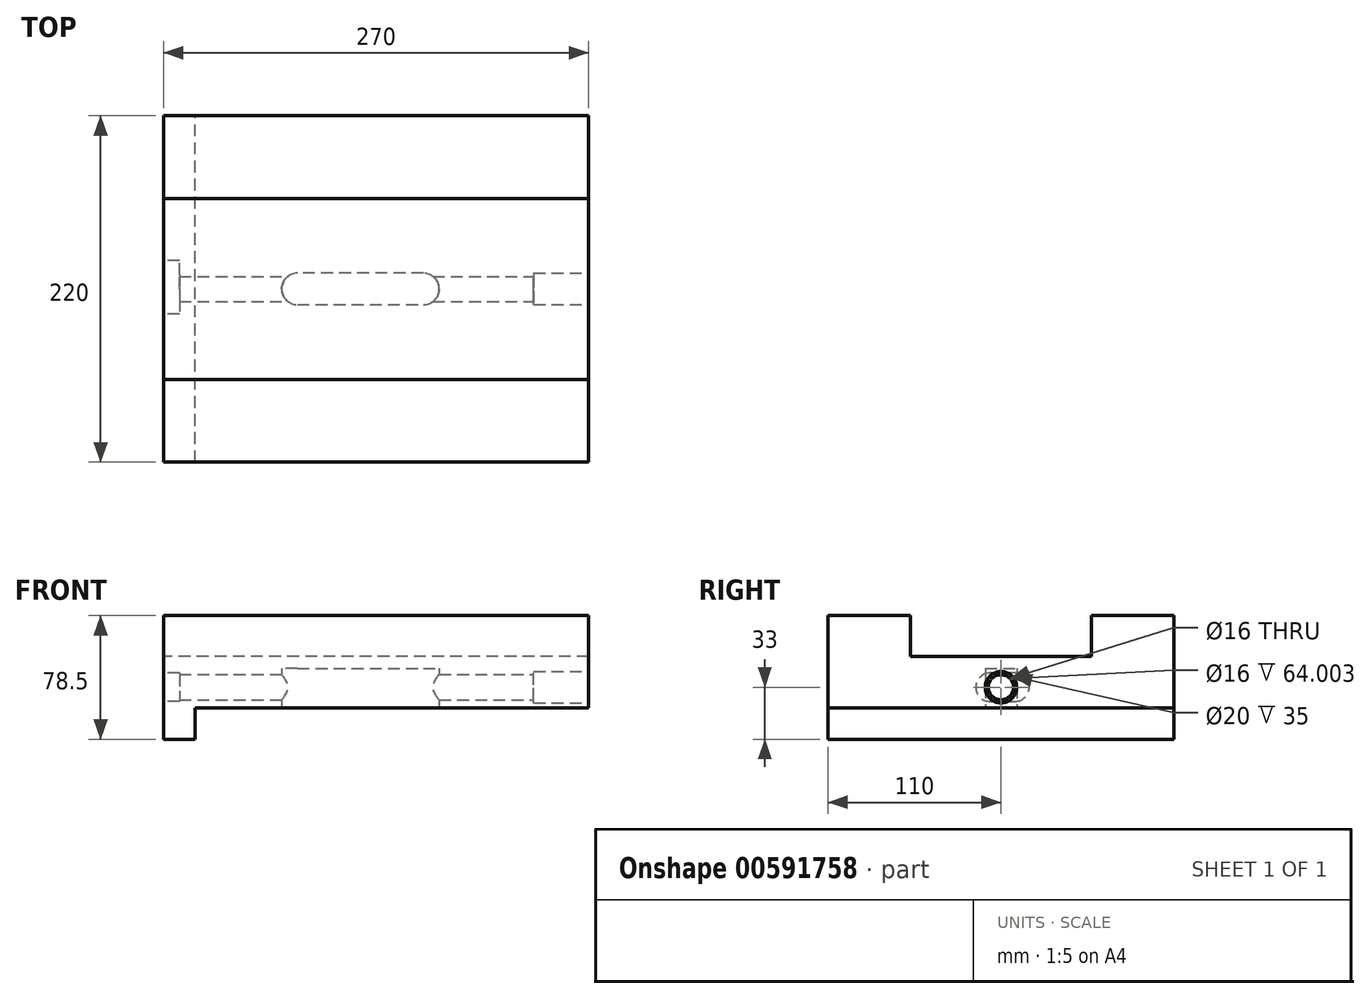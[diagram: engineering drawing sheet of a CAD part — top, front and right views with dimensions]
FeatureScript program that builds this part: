
annotation { "Feature Type Name" : "Feature", "Feature Type Description" : "" }
export const myFeature = defineFeature(function(context is Context, id is Id, definition is map)
    precondition{}
    {
        {
            var Q0;
            Q0=qCreatedBy(makeId("Front.planeOp"),FACE);
            var sketch = newSketch(context, id + "F0", { "sketchPlane" : qUnion([Q0])});
            skLineSegment(sketch, "E0", {"start": v(0, 0) * mm, "end": v(0, 78.5) * mm});
            skLineSegment(sketch, "E1", {"start": v(0, 78.5) * mm, "end": v(270, 78.5) * mm});
            skLineSegment(sketch, "E2", {"start": v(270, 78.5) * mm, "end": v(270, 20) * mm});
            skLineSegment(sketch, "E3", {"start": v(270, 20) * mm, "end": v(20, 20) * mm});
            skLineSegment(sketch, "E4", {"start": v(20, 20) * mm, "end": v(20, 0) * mm});
            skLineSegment(sketch, "E5", {"start": v(20, 0) * mm, "end": v(0, 0) * mm});
            skSolve(sketch);
        }
        {
            var Q0;
            Q0=makeQuery(id+"F0.imprint","IMPRINT",FACE,{"disambiguationData":[TD([[makeQuery(id+"F0.imprint","IMPRINT",EDGE,{"derivedFrom":sQuery(id+"F0.wireOp",EDGE,"E0")}),-1.0]])]});
            extrude(context, id + "F1", {"entities" : qUnion([Q0]), "depth" : (220) * mm, "offsetDistance" : 25 * mm});
        }
        {
            var Q0;
            Q0=makeQuery(id+"F1.opExtrude","SWEPT_FACE",FACE,{"disambiguationData":[OSD([sQuery(id+"F0.wireOp",EDGE,"E2")])]});
            var sketch = newSketch(context, id + "F2", { "sketchPlane" : qUnion([Q0])});
            skCircle(sketch, "E6", {"center": v(-110, 33) * mm, "radius": 8 * mm});
            skCircle(sketch, "E7", {"center": v(-110, 33) * mm, "radius": 10 * mm});
            skSolve(sketch);
        }
        {
            var Q0;
            Q0=makeQuery(id+"F2.imprint","IMPRINT",FACE,{"disambiguationData":[TD([[makeQuery(id+"F2.imprint","IMPRINT",EDGE,{"derivedFrom":sQuery(id+"F2.wireOp",EDGE,"E6")}),1.0]])]});
            extrude(context, id + "F3", {"entities" : qUnion([Q0]), "operationType" : NewBodyOperationType.REMOVE, "endBound" : BoundingType.THROUGH_ALL, "oppositeDirection" : true, "depth" : 25 * mm, "offsetDistance" : 25 * mm});
        }
        {
            var Q0;
            Q0 = qSketchRegion(id + "F2", true);
            extrude(context, id + "F4", {"entities" : qUnion([Q0]), "operationType" : NewBodyOperationType.REMOVE, "oppositeDirection" : true, "depth" : 35 * mm, "offsetDistance" : 25 * mm});
        }
        {
            var Q0;
            Q0=makeQuery(id+"F1.opExtrude","SWEPT_FACE",FACE,{"disambiguationData":[OSD([sQuery(id+"F0.wireOp",EDGE,"E3")])]});
            var sketch = newSketch(context, id + "F5", { "sketchPlane" : qUnion([Q0])});
            skLineSegment(sketch, "E8", {"start": v(85, 120) * mm, "end": v(165, 120) * mm});
            skArc(sketch, "E9", {"start": v(165, 120) * mm, "mid": v(175, 110) * mm, "end": v(165, 100) * mm});
            skLineSegment(sketch, "E10", {"start": v(165, 100) * mm, "end": v(85, 100) * mm});
            skArc(sketch, "E11", {"start": v(85, 100) * mm, "mid": v(75, 110) * mm, "end": v(85, 120) * mm});
            skSolve(sketch);
        }
        {
            var Q0;
            Q0=makeQuery(id+"F5.imprint","IMPRINT",FACE,{"disambiguationData":[TD([[makeQuery(id+"F5.imprint","IMPRINT",EDGE,{"derivedFrom":sQuery(id+"F5.wireOp",EDGE,"E8")}),-1.0]])]});
            extrude(context, id + "F6", {"entities" : qUnion([Q0]), "operationType" : NewBodyOperationType.REMOVE, "oppositeDirection" : true, "depth" : 25 * mm, "offsetDistance" : 25 * mm});
        }
        {
            var Q0;
            Q0=makeQuery(id+"F1.opExtrude","SWEPT_FACE",FACE,{"disambiguationData":[OSD([sQuery(id+"F0.wireOp",EDGE,"E0")])]});
            var sketch = newSketch(context, id + "F7", { "sketchPlane" : qUnion([Q0])});
            skLineSegment(sketch, "E12", {"start": v(101, 42) * mm, "end": v(117, 42) * mm});
            skArc(sketch, "E13", {"start": v(117, 42) * mm, "mid": v(126, 33) * mm, "end": v(117, 24) * mm});
            skLineSegment(sketch, "E14", {"start": v(117, 24) * mm, "end": v(101, 24) * mm});
            skArc(sketch, "E15", {"start": v(101, 24) * mm, "mid": v(92, 33) * mm, "end": v(101, 42) * mm});
            skSolve(sketch);
        }
        {
            var Q0;
            Q0=makeQuery(id+"F7.imprint","IMPRINT",FACE,{"disambiguationData":[TD([[makeQuery(id+"F7.imprint","IMPRINT",EDGE,{"derivedFrom":sQuery(id+"F7.wireOp",EDGE,"E12")}),-1.0]])]});
            extrude(context, id + "F8", {"entities" : qUnion([Q0]), "operationType" : NewBodyOperationType.REMOVE, "oppositeDirection" : true, "depth" : (10) * mm, "offsetDistance" : 25 * mm});
        }
        {
            var Q0;
            Q0=makeQuery(id+"F1.opExtrude","SWEPT_FACE",FACE,{"disambiguationData":[OSD([sQuery(id+"F0.wireOp",EDGE,"E0")])]});
            var sketch = newSketch(context, id + "F9", { "sketchPlane" : qUnion([Q0])});
            skLineSegment(sketch, "E16", {"start": v(52.5, 52.5) * mm, "end": v(167.5, 52.5) * mm});
            skLineSegment(sketch, "E17", {"start": v(167.5, 52.5) * mm, "end": v(167.5, 78.5) * mm});
            skLineSegment(sketch, "E18", {"start": v(167.5, 78.5) * mm, "end": v(52.5, 78.5) * mm});
            skLineSegment(sketch, "E19", {"start": v(52.5, 78.5) * mm, "end": v(52.5, 52.5) * mm});
            skLineSegment(sketch, "E20", {"start": v(110, 0) * mm, "end": v(110, 78.5) * mm, "construction": true});
            skSolve(sketch);
        }
        {
            var Q0;
            Q0=makeQuery(id+"F9.imprint","IMPRINT",FACE,{"disambiguationData":[TD([[makeQuery(id+"F9.imprint","IMPRINT",EDGE,{"derivedFrom":sQuery(id+"F9.wireOp",EDGE,"E16")}),1.0]])]});
            extrude(context, id + "F10", {"entities" : qUnion([Q0]), "operationType" : NewBodyOperationType.REMOVE, "endBound" : BoundingType.THROUGH_ALL, "oppositeDirection" : true, "depth" : 25 * mm, "offsetDistance" : 25 * mm});
        }
    });
